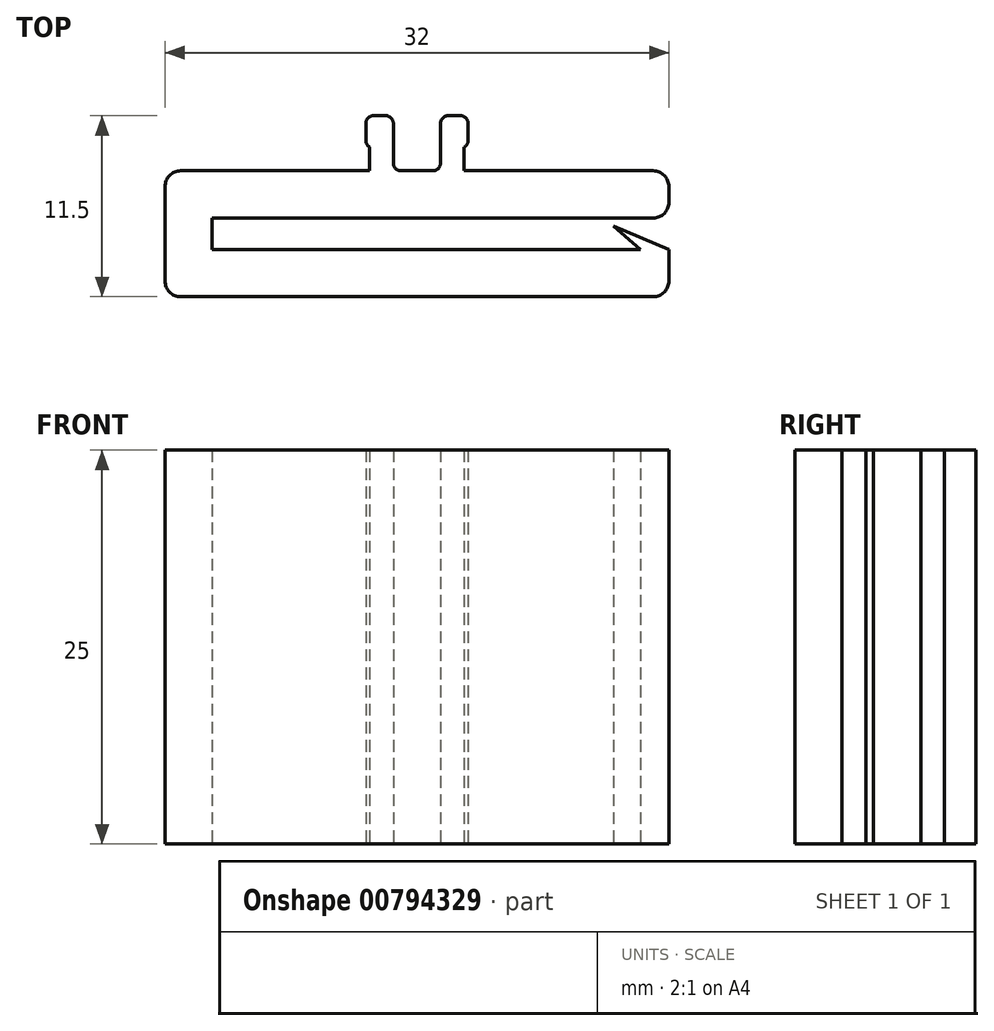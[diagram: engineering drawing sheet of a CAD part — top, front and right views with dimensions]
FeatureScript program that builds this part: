
annotation { "Feature Type Name" : "Feature", "Feature Type Description" : "" }
export const myFeature = defineFeature(function(context is Context, id is Id, definition is map)
    precondition{}
    {
        {
            var Q0;
            Q0=qCreatedBy(makeId("Top.planeOp"),FACE);
            var sketch = newSketch(context, id + "F0", { "sketchPlane" : qUnion([Q0])});
            skLineSegment(sketch, "E0.bottom", {"start": v(0, 0) * mm, "end": v(32, 0) * mm});
            skLineSegment(sketch, "E0.top", {"start": v(0, 8) * mm, "end": v(13, 8) * mm});
            skLineSegment(sketch, "E0.left", {"start": v(0, 0) * mm, "end": v(0, 8) * mm});
            skLineSegment(sketch, "E0.right", {"start": v(32, 0) * mm, "end": v(32, 3) * mm});
            skLineSegment(sketch, "E1.bottom", {"start": v(32, 5) * mm, "end": v(3, 5) * mm});
            skLineSegment(sketch, "E1.top", {"start": v(32, 3) * mm, "end": v(3, 3) * mm});
            skLineSegment(sketch, "E1.right", {"start": v(3, 5) * mm, "end": v(3, 3) * mm});
            skLineSegment(sketch, "E2.trimOffspring", {"start": v(32, 5) * mm, "end": v(32, 8) * mm});
            skLineSegment(sketch, "E3", {"start": v(32, 3) * mm, "end": v(28.48, 4.5) * mm});
            skLineSegment(sketch, "E4", {"start": v(28.48, 4.5) * mm, "end": v(30.2, 3) * mm});
            skLineSegment(sketch, "E5", {"start": v(30.2, 3) * mm, "end": v(32, 3) * mm});
            skLineSegment(sketch, "E6.trimOffspring", {"start": v(19, 8) * mm, "end": v(32, 8) * mm});
            skLineSegment(sketch, "E7.bottom", {"start": v(14.5, 8) * mm, "end": v(17.5, 8) * mm});
            skLineSegment(sketch, "E7.left", {"start": v(13, 8) * mm, "end": v(13, 9.5) * mm});
            skLineSegment(sketch, "E7.right", {"start": v(19, 8) * mm, "end": v(19, 9.5) * mm});
            skLineSegment(sketch, "E8.bottom", {"start": v(12.75, 9.5) * mm, "end": v(13, 9.5) * mm});
            skLineSegment(sketch, "E8.top", {"start": v(12.75, 11.5) * mm, "end": v(14.5, 11.5) * mm});
            skLineSegment(sketch, "E8.left", {"start": v(12.75, 9.5) * mm, "end": v(12.75, 11.5) * mm});
            skLineSegment(sketch, "E8.right", {"start": v(19.25, 9.5) * mm, "end": v(19.25, 11.5) * mm});
            skLineSegment(sketch, "E9.trimOffspring", {"start": v(19, 9.5) * mm, "end": v(19.25, 9.5) * mm});
            skLineSegment(sketch, "E10.left", {"start": v(14.5, 11.5) * mm, "end": v(14.5, 8) * mm});
            skLineSegment(sketch, "E10.right", {"start": v(17.5, 11.5) * mm, "end": v(17.5, 8) * mm});
            skLineSegment(sketch, "E11.trimOffspring", {"start": v(17.5, 11.5) * mm, "end": v(19.25, 11.5) * mm});
            skSolve(sketch);
        }
        {
            var Q0;
            Q0=makeQuery(id+"F0.imprint","IMPRINT",FACE,{"disambiguationData":[TD([[makeQuery(id+"F0.imprint","IMPRINT",EDGE,{"derivedFrom":sQuery(id+"F0.wireOp",EDGE,"E0.bottom")}),1.0]])]});
            var Q1;
            Q1=makeQuery(id+"F0.imprint","IMPRINT",FACE,{"disambiguationData":[TD([[makeQuery(id+"F0.imprint","IMPRINT",EDGE,{"derivedFrom":sQuery(id+"F0.wireOp",EDGE,"E7.bottom")}),1.0]])]});
            var Q2;
            Q2=makeQuery(id+"F0.imprint","IMPRINT",FACE,{"disambiguationData":[TD([[makeQuery(id+"F0.imprint","IMPRINT",EDGE,{"derivedFrom":sQuery(id+"F0.wireOp",EDGE,"E8.top")}),-1.0]])]});
            var Q3;
            Q3=makeQuery(id+"F0.imprint","IMPRINT",FACE,{"disambiguationData":[TD([[makeQuery(id+"F0.imprint","IMPRINT",EDGE,{"derivedFrom":sQuery(id+"F0.wireOp",EDGE,"E3")}),1.0]])]});
            extrude(context, id + "F1", {"entities" : qUnion([Q0, Q1, Q2, Q3]), "depth" : 25 * mm, "offsetDistance" : 25 * mm});
        }
        {
            var Q0;
            Q0=makeQuery(id+"F1.opExtrude","SWEPT_EDGE",EDGE,{"disambiguationData":[OSD([sQuery(id+"F0.wireOp",EDGE,"E2.trimOffspring"),sQuery(id+"F0.wireOp",EDGE,"E6.trimOffspring")])]});
            var Q1;
            Q1=makeQuery(id+"F1.opExtrude","SWEPT_EDGE",EDGE,{"disambiguationData":[OSD([sQuery(id+"F0.wireOp",EDGE,"E1.bottom"),sQuery(id+"F0.wireOp",EDGE,"E2.trimOffspring")])]});
            var Q2;
            Q2=makeQuery(id+"F1.opExtrude","SWEPT_EDGE",EDGE,{"disambiguationData":[OSD([sQuery(id+"F0.wireOp",EDGE,"E0.bottom"),sQuery(id+"F0.wireOp",EDGE,"E0.right")])]});
            var Q3;
            Q3=makeQuery(id+"F1.opExtrude","SWEPT_EDGE",EDGE,{"disambiguationData":[OSD([sQuery(id+"F0.wireOp",EDGE,"E0.bottom"),sQuery(id+"F0.wireOp",EDGE,"E0.left")])]});
            var Q4;
            Q4=makeQuery(id+"F1.opExtrude","SWEPT_EDGE",EDGE,{"disambiguationData":[OSD([sQuery(id+"F0.wireOp",EDGE,"E0.top"),sQuery(id+"F0.wireOp",EDGE,"E0.left")])]});
            fillet(context, id + "F2", {"entities" : qUnion([Q0, Q1, Q2, Q3, Q4]), "radius" : 1 * mm, "tangentPropagation" : true, "allowEdgeOverflow" : false});
        }
        {
            var Q0;
            Q0=makeQuery(id+"F1.opExtrude","SWEPT_EDGE",EDGE,{"disambiguationData":[OSD([sQuery(id+"F0.wireOp",EDGE,"E8.top"),sQuery(id+"F0.wireOp",EDGE,"E8.right")])]});
            var Q1;
            Q1=makeQuery(id+"F1.opExtrude","SWEPT_EDGE",EDGE,{"disambiguationData":[OSD([sQuery(id+"F0.wireOp",EDGE,"E8.right"),sQuery(id+"F0.wireOp",EDGE,"E9.trimOffspring")])]});
            var Q2;
            Q2=makeQuery(id+"F1.opExtrude","SWEPT_EDGE",EDGE,{"disambiguationData":[OSD([sQuery(id+"F0.wireOp",EDGE,"E8.bottom"),sQuery(id+"F0.wireOp",EDGE,"E8.left")])]});
            var Q3;
            Q3=makeQuery(id+"F1.opExtrude","SWEPT_EDGE",EDGE,{"disambiguationData":[OSD([sQuery(id+"F0.wireOp",EDGE,"E8.top"),sQuery(id+"F0.wireOp",EDGE,"E8.left")])]});
            var Q4;
            Q4=makeQuery(id+"F1.opExtrude","SWEPT_EDGE",EDGE,{"disambiguationData":[OSD([sQuery(id+"F0.wireOp",EDGE,"E8.top"),sQuery(id+"F0.wireOp",EDGE,"E10.bottom"),sQuery(id+"F0.wireOp",EDGE,"E10.left")])]});
            var Q5;
            Q5=makeQuery(id+"F1.opExtrude","SWEPT_EDGE",EDGE,{"disambiguationData":[OSD([sQuery(id+"F0.wireOp",EDGE,"E8.top"),sQuery(id+"F0.wireOp",EDGE,"E10.bottom"),sQuery(id+"F0.wireOp",EDGE,"E10.right")])]});
            var Q6;
            Q6=makeQuery(id+"F1.opExtrude","SWEPT_EDGE",EDGE,{"disambiguationData":[OSD([sQuery(id+"F0.wireOp",EDGE,"E7.bottom"),sQuery(id+"F0.wireOp",EDGE,"E10.left")])]});
            fillet(context, id + "F3", {"entities" : qUnion([Q0, Q1, Q2, Q3, Q4, Q5, Q6]), "radius" : .5 * mm, "tangentPropagation" : true, "allowEdgeOverflow" : false});
        }
    });
